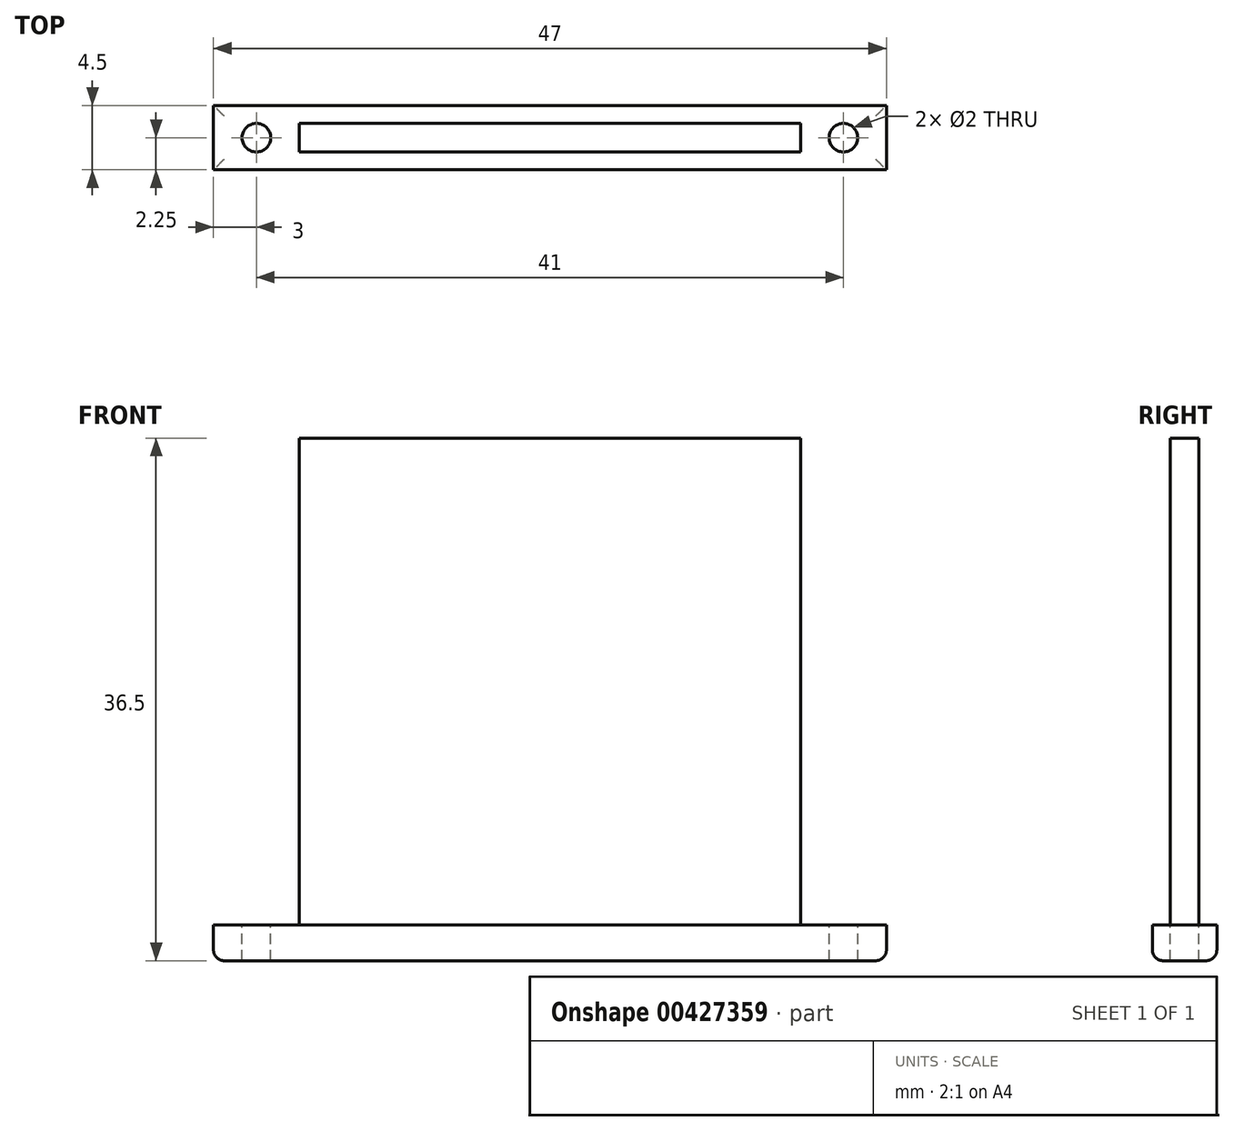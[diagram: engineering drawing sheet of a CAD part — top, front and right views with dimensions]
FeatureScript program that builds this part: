
annotation { "Feature Type Name" : "Feature", "Feature Type Description" : "" }
export const myFeature = defineFeature(function(context is Context, id is Id, definition is map)
    precondition{}
    {
        {
            var Q0;
            Q0=qCreatedBy(makeId("Top.planeOp"),FACE);
            var sketch = newSketch(context, id + "F0", { "sketchPlane" : qUnion([Q0])});
            skLineSegment(sketch, "E0.bottom", {"start": v(0, 0) * mm, "end": v(35, 0) * mm});
            skLineSegment(sketch, "E0.top", {"start": v(0, 2) * mm, "end": v(35, 2) * mm});
            skLineSegment(sketch, "E0.left", {"start": v(0, 0) * mm, "end": v(0, 2) * mm});
            skLineSegment(sketch, "E0.right", {"start": v(35, 0) * mm, "end": v(35, 2) * mm});
            skSolve(sketch);
        }
        {
            var Q0;
            Q0 = qSketchRegion(id + "F0", true);
            extrude(context, id + "F1", {"entities" : qUnion([Q0]), "depth" : 34 * mm});
        }
        {
            var Q0;
            Q0=qCreatedBy(makeId("Top.planeOp"),FACE);
            var sketch = newSketch(context, id + "F2", { "sketchPlane" : qUnion([Q0])});
            skLineSegment(sketch, "E1.bottom", {"start": v(-6, -1.25) * mm, "end": v(41, -1.25) * mm});
            skLineSegment(sketch, "E1.top", {"start": v(-6, 3.25) * mm, "end": v(41, 3.25) * mm});
            skLineSegment(sketch, "E1.left", {"start": v(-6, -1.25) * mm, "end": v(-6, 3.25) * mm});
            skLineSegment(sketch, "E1.right", {"start": v(41, -1.25) * mm, "end": v(41, 3.25) * mm});
            skCircle(sketch, "E2", {"center": v(-3, 1) * mm, "radius": 1 * mm});
            skCircle(sketch, "E3", {"center": v(38, 1) * mm, "radius": 1 * mm});
            skSolve(sketch);
        }
        {
            var Q0;
            Q0=makeQuery(id+"F2.imprint","IMPRINT",FACE,{"disambiguationData":[TD([[makeQuery(id+"F2.imprint","IMPRINT",EDGE,{"derivedFrom":sQuery(id+"F2.wireOp",EDGE,"E1.bottom")}),1.0]])]});
            extrude(context, id + "F3", {"entities" : qUnion([Q0]), "operationType" : NewBodyOperationType.ADD, "oppositeDirection" : true, "depth" : 2.5 * mm});
        }
        {
            var Q0;
            Q0=makeQuery(id+"F3.opExtrude","CAP_EDGE",EDGE,{"disambiguationData":[OSD([sQuery(id+"F2.wireOp",EDGE,"E1.left")])],"isStart":false});
            var Q1;
            Q1=makeQuery(id+"F3.opExtrude","CAP_EDGE",EDGE,{"disambiguationData":[OSD([sQuery(id+"F2.wireOp",EDGE,"E1.bottom")])],"isStart":false});
            var Q2;
            Q2=makeQuery(id+"F3.opExtrude","CAP_EDGE",EDGE,{"disambiguationData":[OSD([sQuery(id+"F2.wireOp",EDGE,"E1.right")])],"isStart":false});
            var Q3;
            Q3=makeQuery(id+"F3.opExtrude","CAP_EDGE",EDGE,{"disambiguationData":[OSD([sQuery(id+"F2.wireOp",EDGE,"E1.top")])],"isStart":false});
            fillet(context, id + "F4", {"entities" : qUnion([Q0, Q1, Q2, Q3]), "radius" : .74 * mm, "tangentPropagation" : true, "allowEdgeOverflow" : false});
        }
    });
